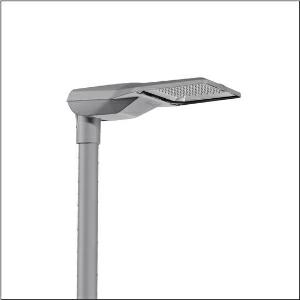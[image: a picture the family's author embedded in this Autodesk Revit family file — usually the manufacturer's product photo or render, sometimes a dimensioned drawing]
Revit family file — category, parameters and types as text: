
# Revit family: streetlight_sl_21_iq_midi___st1_0a_5xe3d31g08mb_3419
name_source: partatom
category: Lighting Fixtures
units: mm (PartAtom-declared; Revit-internal decimal feet)

## family parameters
Cut with Voids When Loaded = No
Host = Face
Light Source = No
Part Type = Normal
Room Calculation Point = No
Round Connector Dimension = Use Diameter
Shared = No

## types (1)
- --- (1 x LED, 19500 lm, 146.7 W, 3000K)
    Apparent Load = 147 VA
    CIE Flux Codes = 37 72 97 100 100
    Color Rendering = 70
    Color Temperature = 3000K
    Default Elevation = 1800 mm
    Description = Streetlight SL 21 iQ midi, mast luminaire, primary light control with lens, of PMMA, primary optical cover: cover, of toughened safety glass, transparent, light distribution: ST1.0a, light emission: direct distribution, primary light characteristic: asymmetric, installation type: post-top, side-entry, LED, High Power LED, rated luminous flux: 19.500lm, luminous efficacy: 133lm/W, light colour: 730, colour temperature: 3000K, control: Street-Remote, Auto-Match, Temp-Guard, Lumen-Switch, Night-Set, Smart-Wire, Light-Fading, Desk-Remote (wireless, voltage-free reading and setting of iQ features in the workshop via application-optimized NFC function/RFID function), optimised constant luminous flux control (CLO 2.0), presetting dimming linear, mains connection: 230..240V, AC, 50/60Hz, start of lifetime: 147W, end of service life: 161W, reduction: 62W, luminaire housing, of diecast aluminium, powder-coated, Siteco® metallic grey (DB 702S), corrosivity category C5 mid according to DIN EN ISO 12944, please order mast flange separately, inclination adjustable: 0°, 5°, 10°, 15°, sealing non-destructively replaceable, multi-level sealing system, length: 644mm, width: 335mm, height: 110mm, mast flange for spigot size: 42mm (side-entry): 5XC10008XM4, 60/48mm (side-entry/post-top): 5XC10108XM2, 76/60mm (side-entry/post-top): 5XC10108XM1, protection rating (complete): IP66, insulation class (complete): insulation class II (safety insulation), certification: CE, ENEC, ENEC+, VDE, impact resistance: IK09, permissible operating ambient temperature for outdoor applications: -40..+50°C, standard-compliant lighting for roads and squares, packaging unit: 1 piece

Light Distribution: ST1.0a
    Height = 111 mm
    Lamp = 1 x LED
    Lamp Light Flux = 19500 lm
    Lamp Power = 146.7 W
    Lamp count = 1
    Length = 644 mm
    Luminous efficacy = 133 lm/W
    Manufacturer = Siteco
    ModVariant = No
    Model = 5XE3D31G08MB
    Number of Poles = 1
    OnlyDefault = Yes
    Power Factor = 1
    Product Name = Streetlight SL 21 iQ midi | ST1.0a
    Product group = mast luminaire | pylon top
    ProductGroupID = 6100
    Protection Class = Protection class II
    Protection Degree = IP 66
    RLX_Detail_Level = 1
    RLX_Emergency_Light_Flux = 0 lm
    RLX_Emergency_Type = 0
    RLX_Emergency_Type_DB = No
    RlxData = <blob elided: 90705 chars, md5=fa32e9d0>
    Socket = socket
    Standby Power = 0 W
    System Light Flux = 19499 lm
    System Power = 147 W
    Type Comments = factory setting: luminous flux: 100 % | dim-lin: 254 | 753 mA
    Type Image = l_1004298.jpg
    URL = http://relux.com
    VarID = @adj_123487
    Voltage = 0 V
    Weight = 0.00 kg
    Width = 336 mm

## geometry (parser evidence)
native form markers: Blend x4, Sweep x11
no freeform markers — native parametric forms only
